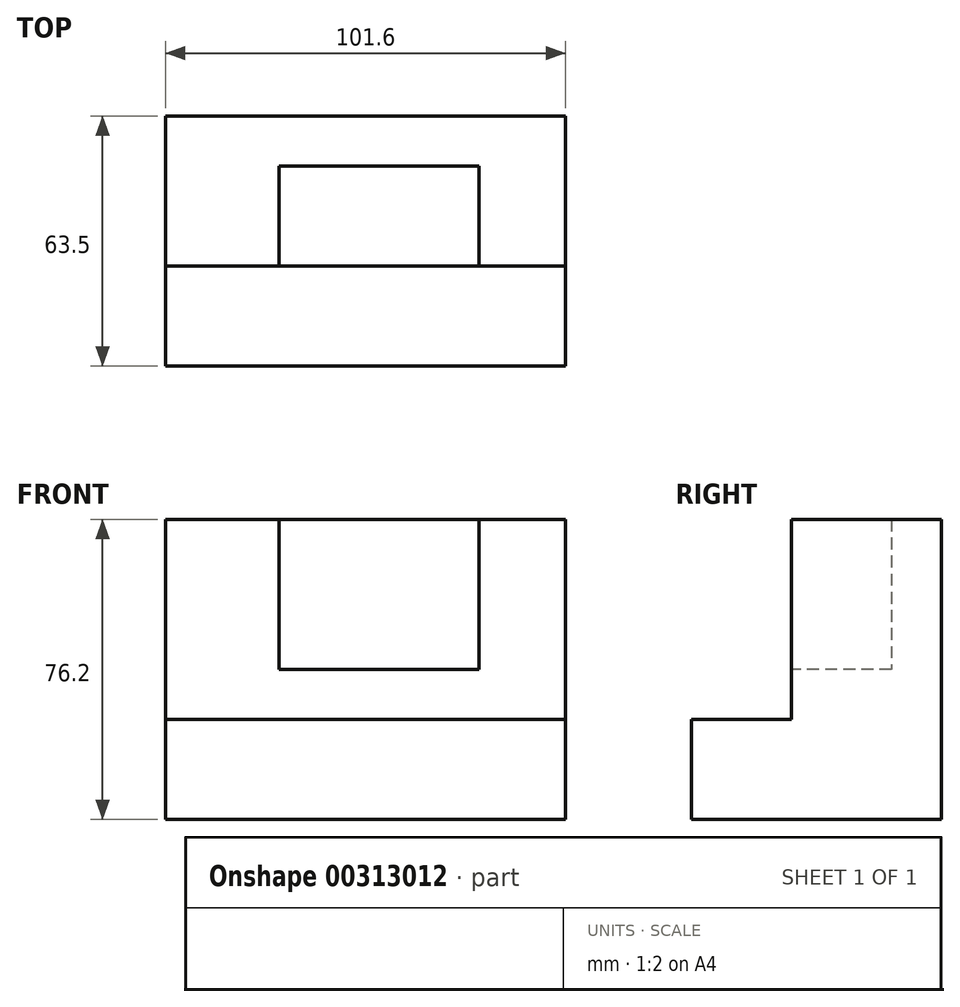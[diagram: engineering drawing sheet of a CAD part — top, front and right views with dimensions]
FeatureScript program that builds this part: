
annotation { "Feature Type Name" : "Feature", "Feature Type Description" : "" }
export const myFeature = defineFeature(function(context is Context, id is Id, definition is map)
    precondition{}
    {
        {
            var Q0;
            Q0=qCreatedBy(makeId("Right.planeOp"),FACE);
            var sketch = newSketch(context, id + "F0", { "sketchPlane" : qUnion([Q0])});
            skLineSegment(sketch, "E0", {"start": v(-26.8, -26.85) * mm, "end": v(36.7, -26.85) * mm});
            skLineSegment(sketch, "E1", {"start": v(36.7, -26.85) * mm, "end": v(36.7, 49.35) * mm});
            skLineSegment(sketch, "E2", {"start": v(36.7, 49.35) * mm, "end": v(-1.4, 49.35) * mm});
            skLineSegment(sketch, "E3", {"start": v(-1.4, 49.35) * mm, "end": v(-1.4, -1.45) * mm});
            skLineSegment(sketch, "E4", {"start": v(-1.4, -1.45) * mm, "end": v(-26.8, -1.45) * mm});
            skLineSegment(sketch, "E5", {"start": v(-26.8, -1.45) * mm, "end": v(-26.8, -26.85) * mm});
            skSolve(sketch);
        }
        {
            var Q0;
            Q0=makeQuery(id+"F0.imprint","IMPRINT",FACE,{"disambiguationData":[TD([[makeQuery(id+"F0.imprint","IMPRINT",EDGE,{"derivedFrom":sQuery(id+"F0.wireOp",EDGE,"E0")}),1.0]])]});
            extrude(context, id + "F1", {"entities" : qUnion([Q0]), "oppositeDirection" : true, "depth" : 101.6 * mm});
        }
        {
            var Q0;
            Q0=makeQuery(id+"F1.opExtrude","SWEPT_FACE",FACE,{"disambiguationData":[OSD([sQuery(id+"F0.wireOp",EDGE,"E3")])]});
            var sketch = newSketch(context, id + "F2", { "sketchPlane" : qUnion([Q0])});
            skLineSegment(sketch, "E6", {"start": v(-72.75, 49.35) * mm, "end": v(-72.75, 11.25) * mm});
            skLineSegment(sketch, "E7", {"start": v(-72.75, 11.25) * mm, "end": v(-21.95, 11.25) * mm});
            skLineSegment(sketch, "E8", {"start": v(-21.95, 11.25) * mm, "end": v(-21.95, 49.35) * mm});
            skLineSegment(sketch, "E9", {"start": v(-72.75, 49.35) * mm, "end": v(-21.95, 49.35) * mm});
            skSolve(sketch);
        }
        {
            var Q0;
            Q0=makeQuery(id+"F2.imprint","IMPRINT",FACE,{"disambiguationData":[TD([[makeQuery(id+"F2.imprint","IMPRINT",EDGE,{"derivedFrom":sQuery(id+"F2.wireOp",EDGE,"E6")}),1.0]])]});
            extrude(context, id + "F3", {"entities" : qUnion([Q0]), "operationType" : NewBodyOperationType.REMOVE, "oppositeDirection" : true, "depth" : 25.4 * mm});
        }
    });
